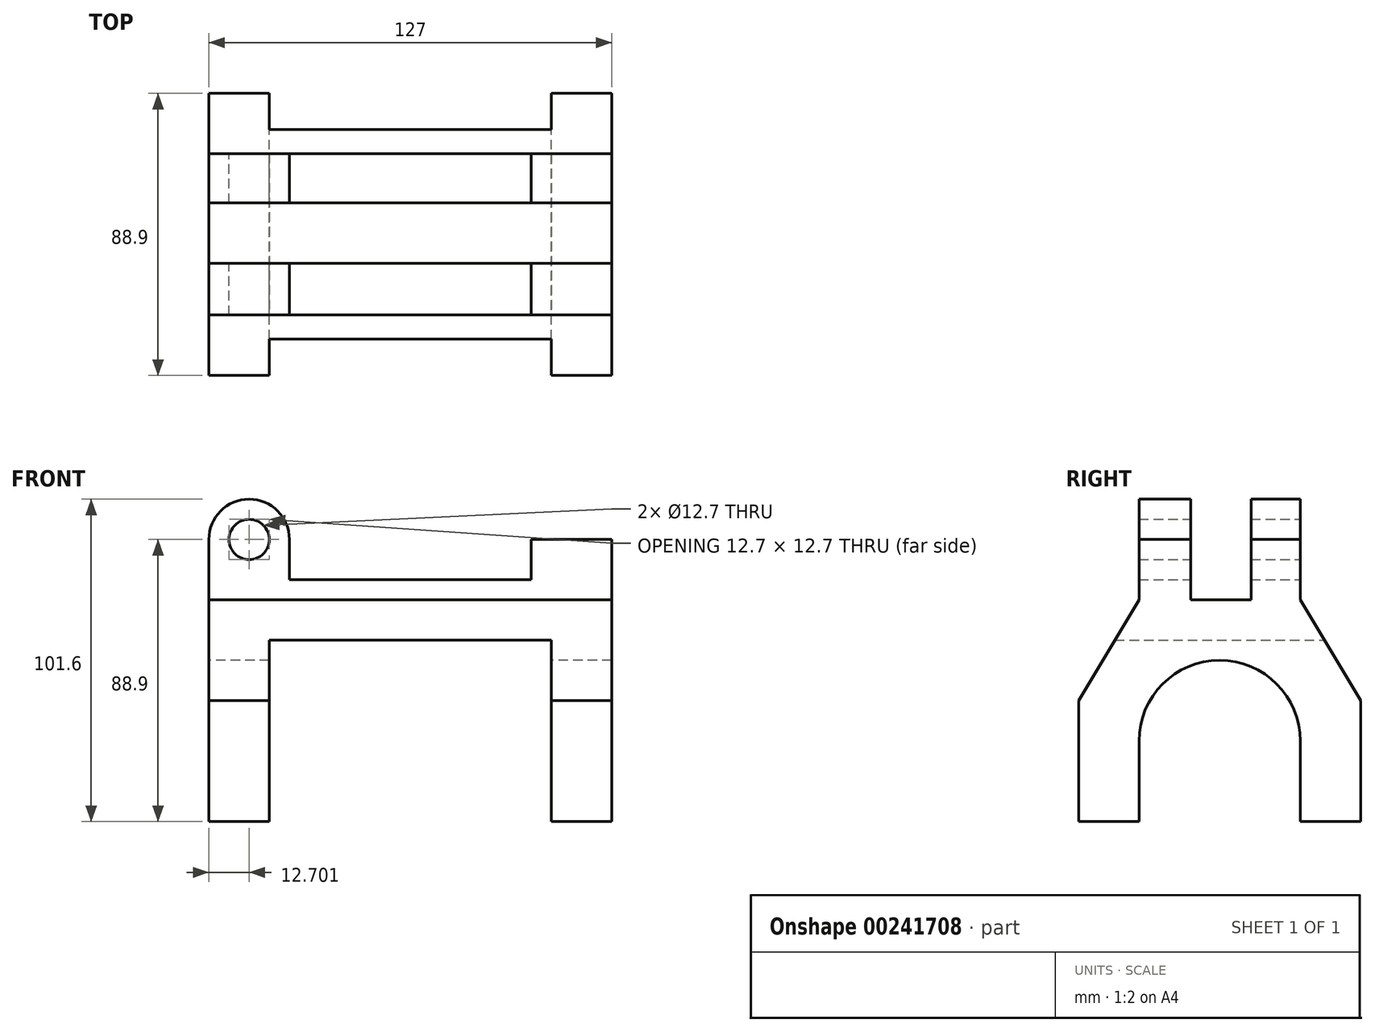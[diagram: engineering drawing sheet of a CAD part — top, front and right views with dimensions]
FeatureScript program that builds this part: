
annotation { "Feature Type Name" : "Feature", "Feature Type Description" : "" }
export const myFeature = defineFeature(function(context is Context, id is Id, definition is map)
    precondition{}
    {
        {
            var Q0;
            Q0=qCreatedBy(makeId("Front.planeOp"),FACE);
            var sketch = newSketch(context, id + "F0", { "sketchPlane" : qUnion([Q0])});
            skLineSegment(sketch, "E0.top", {"start": v(-38.24, -43.04) * mm, "end": v(-19.19, -43.04) * mm});
            skLineSegment(sketch, "E0.left", {"start": v(-38.24, 14.1) * mm, "end": v(-38.24, -43.04) * mm});
            skLineSegment(sketch, "E0.right", {"start": v(-19.19, 14.1) * mm, "end": v(-19.19, -43.04) * mm});
            skLineSegment(sketch, "E1.bottom", {"start": v(-19.19, 14.1) * mm, "end": v(69.71, 14.1) * mm});
            skLineSegment(sketch, "E1.top", {"start": v(-12.84, 33.16) * mm, "end": v(63.36, 33.16) * mm});
            skLineSegment(sketch, "E1.left", {"start": v(-38.24, 14.1) * mm, "end": v(-38.24, 33.16) * mm});
            skLineSegment(sketch, "E1.right", {"start": v(88.76, 14.1) * mm, "end": v(88.76, 33.16) * mm});
            skLineSegment(sketch, "E2.top", {"start": v(88.76, -43.04) * mm, "end": v(69.71, -43.04) * mm});
            skLineSegment(sketch, "E2.left", {"start": v(88.76, 14.1) * mm, "end": v(88.76, -43.04) * mm});
            skLineSegment(sketch, "E2.right", {"start": v(69.71, 14.1) * mm, "end": v(69.71, -43.04) * mm});
            skLineSegment(sketch, "E3.top", {"start": v(88.76, 45.86) * mm, "end": v(63.36, 45.86) * mm});
            skLineSegment(sketch, "E3.left", {"start": v(88.76, 33.16) * mm, "end": v(88.76, 45.86) * mm});
            skLineSegment(sketch, "E3.right", {"start": v(63.36, 33.16) * mm, "end": v(63.36, 45.86) * mm});
            skArc(sketch, "E4", {"start": v(-12.84, 45.86) * mm, "mid": v(-25.54, 58.56) * mm, "end": v(-38.24, 45.86) * mm});
            skCircle(sketch, "E5", {"center": v(-25.54, 45.86) * mm, "radius": 6.35 * mm});
            skLineSegment(sketch, "E6", {"start": v(-38.24, 45.86) * mm, "end": v(-38.24, 33.16) * mm});
            skLineSegment(sketch, "E7", {"start": v(-12.84, 45.86) * mm, "end": v(-12.84, 33.16) * mm});
            skSolve(sketch);
        }
        {
            var Q0;
            Q0 = qSketchRegion(id + "F0", true);
            extrude(context, id + "F1", {"entities" : qUnion([Q0]), "depth" : 88.9 * mm});
        }
        {
            var Q0;
            Q0=makeQuery(id+"F1.opExtrude","SWEPT_FACE",FACE,{"disambiguationData":[OSD([sQuery(id+"F0.wireOp",EDGE,"E0.left"),sQuery(id+"F0.wireOp",EDGE,"E1.left"),sQuery(id+"F0.wireOp",EDGE,"E6")])]});
            var sketch = newSketch(context, id + "F2", { "sketchPlane" : qUnion([Q0])});
            skPoint(sketch, "E8.centerSnap0", {"position": v(44.45, -43.04) * mm});
            skLineSegment(sketch, "E9", {"start": v(19.05, -17.64) * mm, "end": v(19.05, -43.04) * mm});
            skLineSegment(sketch, "E10", {"start": v(69.85, -17.64) * mm, "end": v(69.85, -43.04) * mm});
            skArc(sketch, "E11", {"start": v(69.85, -17.64) * mm, "mid": v(44.45, 7.76) * mm, "end": v(19.05, -17.64) * mm});
            skLineSegment(sketch, "E12", {"start": v(88.9, -4.94) * mm, "end": v(69.85, 26.8) * mm});
            skLineSegment(sketch, "E13", {"start": v(0, -4.94) * mm, "end": v(19.05, 26.8) * mm});
            skLineSegment(sketch, "E14", {"start": v(19.05, 26.8) * mm, "end": v(19.05, 58.56) * mm});
            skLineSegment(sketch, "E15", {"start": v(69.85, 58.56) * mm, "end": v(69.85, 26.8) * mm});
            skLineSegment(sketch, "E16", {"start": v(44.45, 26.8) * mm, "end": v(53.58, 26.8) * mm});
            skLineSegment(sketch, "E17", {"start": v(34.53, 26.8) * mm, "end": v(44.45, 26.8) * mm});
            skLineSegment(sketch, "E18", {"start": v(34.53, 58.56) * mm, "end": v(34.53, 26.8) * mm});
            skLineSegment(sketch, "E19", {"start": v(53.58, 26.8) * mm, "end": v(53.58, 58.56) * mm});
            skPoint(sketch, "E20.start.orphan", {"position": v(44.45, 61.13) * mm});
            skPoint(sketch, "E21.orphan", {"position": v(19.05, 61.13) * mm});
            skPoint(sketch, "E22.orphan", {"position": v(53.58, 61.13) * mm});
            skPoint(sketch, "E23.orphan", {"position": v(69.85, 61.13) * mm});
            skPoint(sketch, "E24.start.orphan", {"position": v(88.9, 45.86) * mm});
            skPoint(sketch, "E25.orphan", {"position": v(88.9, 58.56) * mm});
            skLineSegment(sketch, "E26", {"start": v(19.05, 58.56) * mm, "end": v(0, 58.56) * mm});
            skLineSegment(sketch, "E27", {"start": v(0, 58.56) * mm, "end": v(0, -4.94) * mm});
            skLineSegment(sketch, "E28", {"start": v(69.85, 58.56) * mm, "end": v(88.9, 58.56) * mm});
            skLineSegment(sketch, "E29", {"start": v(88.9, -4.94) * mm, "end": v(88.9, 58.56) * mm});
            skLineSegment(sketch, "E30", {"start": v(34.53, 58.56) * mm, "end": v(53.58, 58.56) * mm});
            skSolve(sketch);
        }
        {
            var Q0;
            Q0 = qSketchRegion(id + "F2", true);
            var Q1;
            {var subQ0=sQuery(id+"F2.wireOp",EDGE,"E9");Q1=makeQuery(id+"F2.imprint","IMPRINT",FACE,{"disambiguationData":[TD([[makeQuery(id+"F2.imprint","IMPRINT",EDGE,{"derivedFrom":subQ0}),1.0]])]});}
            extrude(context, id + "F3", {"entities" : qUnion([Q0, Q1]), "operationType" : NewBodyOperationType.REMOVE, "endBound" : BoundingType.THROUGH_ALL, "oppositeDirection" : true, "depth" : 127 * mm});
        }
    });
